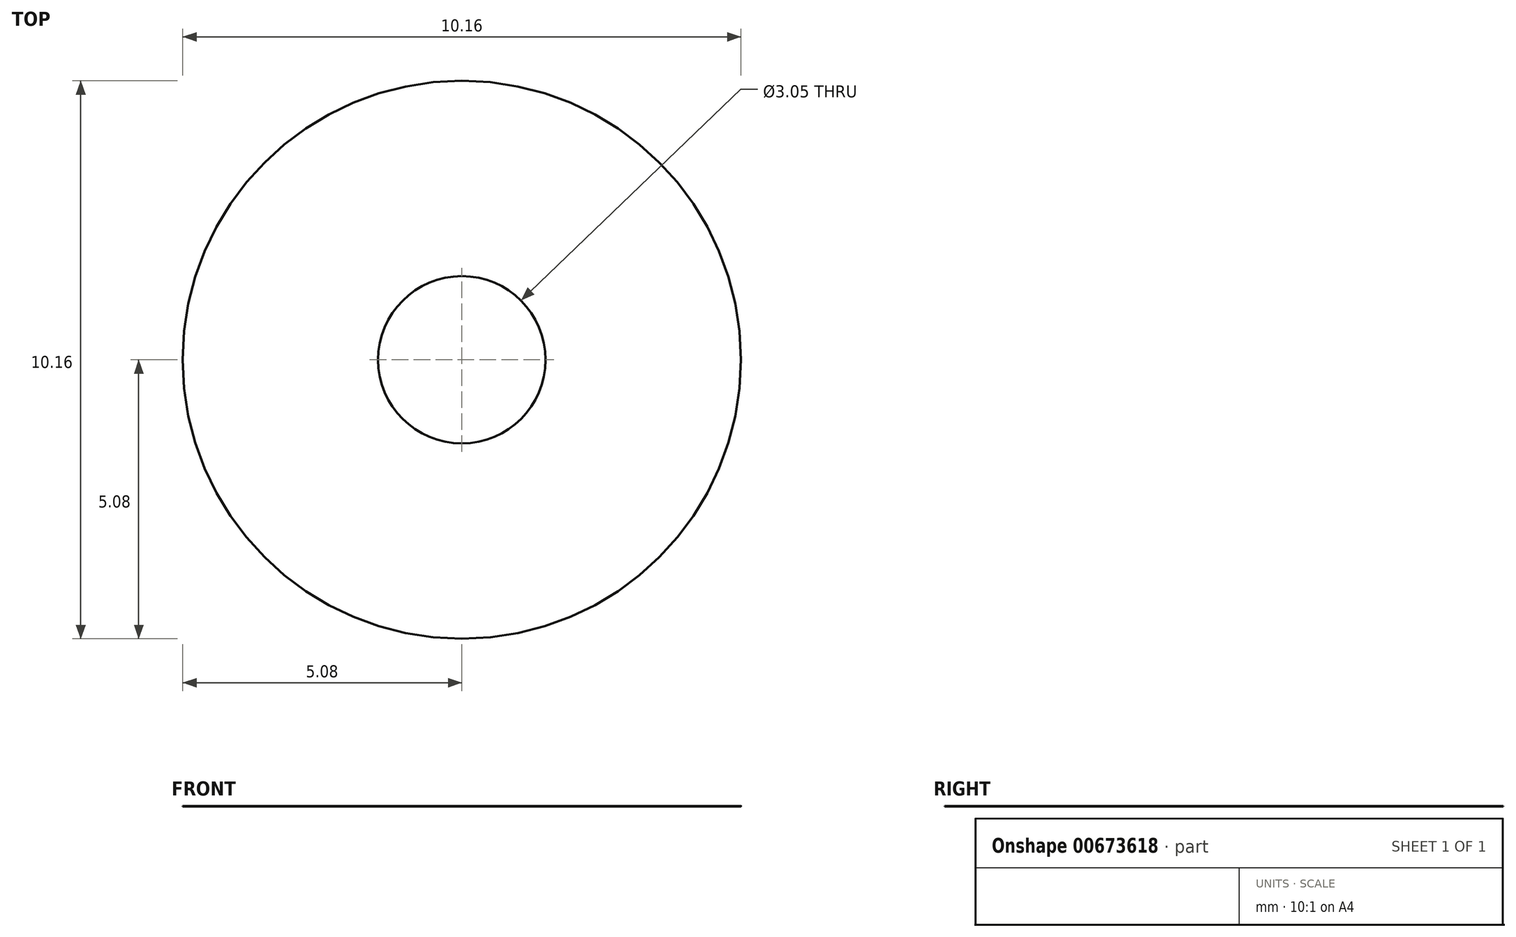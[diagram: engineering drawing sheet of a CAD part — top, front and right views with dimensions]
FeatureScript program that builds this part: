
annotation { "Feature Type Name" : "Feature", "Feature Type Description" : "" }
export const myFeature = defineFeature(function(context is Context, id is Id, definition is map)
    precondition{}
    {
        {
            var Q0;
            Q0=qCreatedBy(makeId("Top.planeOp"),FACE);
            var sketch = newSketch(context, id + "F0", { "sketchPlane" : qUnion([Q0])});
            skCircle(sketch, "E0", {"center": v(0, 0) * mm, "radius": 5.08 * mm});
            skCircle(sketch, "E1", {"center": v(0, 0) * mm, "radius": 1.52 * mm});
            skSolve(sketch);
        }
        {
            var Q0;
            Q0=makeQuery(id+"F0.imprint","IMPRINT",FACE,{"disambiguationData":[TD([[makeQuery(id+"F0.imprint","IMPRINT",EDGE,{"derivedFrom":sQuery(id+"F0.wireOp",EDGE,"E0")}),1.0]])]});
            extrude(context, id + "F1", {"entities" : qUnion([Q0]), "depth" : 1 / 203.2 * mm});
        }
    });
